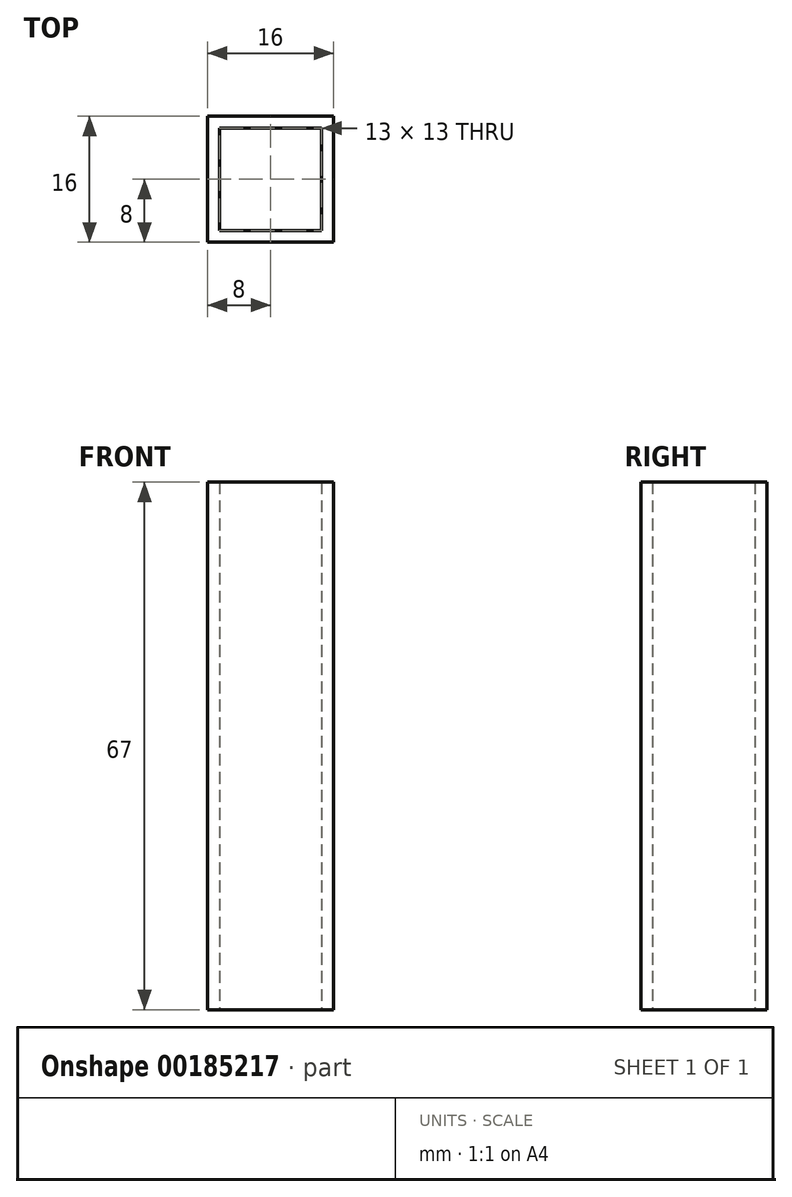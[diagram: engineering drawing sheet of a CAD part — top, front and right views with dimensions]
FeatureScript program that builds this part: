
annotation { "Feature Type Name" : "Feature", "Feature Type Description" : "" }
export const myFeature = defineFeature(function(context is Context, id is Id, definition is map)
    precondition{}
    {
        {
            var Q0;
            Q0=qCreatedBy(makeId("Top.planeOp"),FACE);
            var sketch = newSketch(context, id + "F0", { "sketchPlane" : qUnion([Q0])});
            skLineSegment(sketch, "E0.bottom", {"start": v(8, 8) * mm, "end": v(-8, 8) * mm});
            skLineSegment(sketch, "E0.top", {"start": v(8, -8) * mm, "end": v(-8, -8) * mm});
            skLineSegment(sketch, "E0.left", {"start": v(8, 8) * mm, "end": v(8, -8) * mm});
            skLineSegment(sketch, "E0.right", {"start": v(-8, 8) * mm, "end": v(-8, -8) * mm});
            skPoint(sketch, "E0.middle", {"position": v(0, 0) * mm});
            skLineSegment(sketch, "E1.0", {"start": v(6.5, 6.5) * mm, "end": v(-6.5, 6.5) * mm});
            skLineSegment(sketch, "E2.0", {"start": v(6.5, 6.5) * mm, "end": v(6.5, -6.5) * mm});
            skLineSegment(sketch, "E3.0", {"start": v(6.5, -6.5) * mm, "end": v(-6.5, -6.5) * mm});
            skLineSegment(sketch, "E4.0", {"start": v(-6.5, 6.5) * mm, "end": v(-6.5, -6.5) * mm});
            skSolve(sketch);
        }
        {
            var Q0;
            Q0=makeQuery(id+"F0.imprint","IMPRINT",FACE,{"disambiguationData":[TD([[makeQuery(id+"F0.imprint","IMPRINT",EDGE,{"derivedFrom":sQuery(id+"F0.wireOp",EDGE,"E0.bottom")}),1.0]])]});
            extrude(context, id + "F1", {"entities" : qUnion([Q0]), "depth" : (75 - 8) * mm, "offsetDistance" : 25 * mm});
        }
    });
